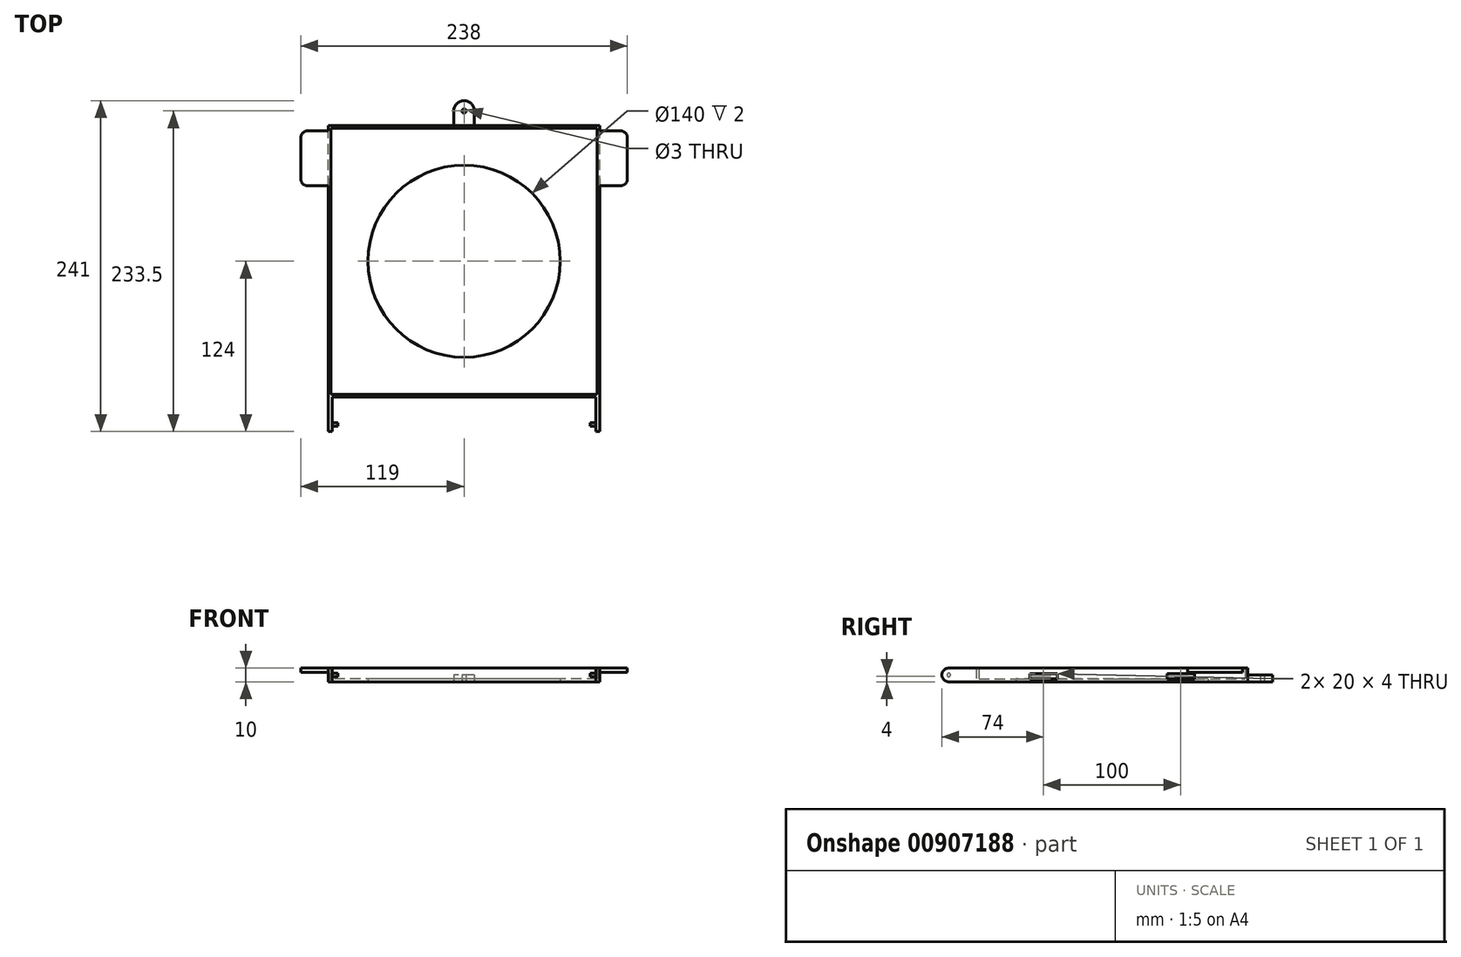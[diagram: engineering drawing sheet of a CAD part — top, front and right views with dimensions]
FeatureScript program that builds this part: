
annotation { "Feature Type Name" : "Feature", "Feature Type Description" : "" }
export const myFeature = defineFeature(function(context is Context, id is Id, definition is map)
    precondition{}
    {
        {
            var Q0;
            Q0=qCreatedBy(makeId("Top.planeOp"),FACE);
            var sketch = newSketch(context, id + "F0", { "sketchPlane" : qUnion([Q0])});
            skLineSegment(sketch, "E0.bottom", {"start": v(97, -97) * mm, "end": v(-97, -97) * mm});
            skLineSegment(sketch, "E0.top", {"start": v(97, 97) * mm, "end": v(-97, 97) * mm});
            skLineSegment(sketch, "E0.left", {"start": v(97, -97) * mm, "end": v(97, 97) * mm});
            skLineSegment(sketch, "E0.right", {"start": v(-97, -97) * mm, "end": v(-97, 97) * mm});
            skPoint(sketch, "E0.middle", {"position": v(0, 0) * mm});
            skLineSegment(sketch, "E1.bottom", {"start": v(99, -99) * mm, "end": v(-99, -99) * mm});
            skLineSegment(sketch, "E1.top", {"start": v(99, 99) * mm, "end": v(-99, 99) * mm});
            skLineSegment(sketch, "E1.left", {"start": v(99, -99) * mm, "end": v(99, 99) * mm});
            skLineSegment(sketch, "E1.right", {"start": v(-99, -99) * mm, "end": v(-99, 99) * mm});
            skCircle(sketch, "E2", {"center": v(0, 0) * mm, "radius": 70 * mm});
            skLineSegment(sketch, "E3.bottom", {"start": v(-99, -99) * mm, "end": v(-96, -99) * mm});
            skLineSegment(sketch, "E3.top", {"start": v(-99, -119) * mm, "end": v(-96, -119) * mm});
            skLineSegment(sketch, "E3.left", {"start": v(-99, -99) * mm, "end": v(-99, -119) * mm});
            skLineSegment(sketch, "E3.right", {"start": v(-96, -99) * mm, "end": v(-96, -119) * mm});
            skLineSegment(sketch, "E4.MirrorCS", {"start": v(99, -99) * mm, "end": v(99, -119) * mm});
            skLineSegment(sketch, "E5.MirrorCS", {"start": v(96, -99) * mm, "end": v(96, -119) * mm});
            skLineSegment(sketch, "E6.MirrorCS", {"start": v(99, -119) * mm, "end": v(96, -119) * mm});
            skLineSegment(sketch, "E7.bottom", {"start": v(-7.5, 99) * mm, "end": v(7.5, 99) * mm});
            skLineSegment(sketch, "E7.left", {"start": v(-7.5, 99) * mm, "end": v(-7.5, 109.5) * mm});
            skLineSegment(sketch, "E7.right", {"start": v(7.5, 99) * mm, "end": v(7.5, 109.5) * mm});
            skArc(sketch, "E8", {"start": v(7.5, 109.5) * mm, "mid": v(0, 117) * mm, "end": v(-7.5, 109.5) * mm});
            skCircle(sketch, "E9", {"center": v(0, 109.5) * mm, "radius": 1.5 * mm});
            skSolve(sketch);
        }
        {
            var Q0;
            Q0=makeQuery(id+"F0.imprint","IMPRINT",FACE,{"disambiguationData":[TD([[makeQuery(id+"F0.imprint","IMPRINT",EDGE,{"derivedFrom":sQuery(id+"F0.wireOp",EDGE,"E0.bottom")}),-1.0]])]});
            extrude(context, id + "F1", {"entities" : qUnion([Q0]), "depth" : 2 * mm});
        }
        {
            var Q0;
            {var subQ1=sQuery(id+"F0.wireOp",EDGE,"E7.left");Q0=makeQuery(id+"F0.imprint","IMPRINT",FACE,{"disambiguationData":[TD([[makeQuery(id+"F0.imprint","IMPRINT",EDGE,{"derivedFrom":subQ1}),-1.0]])]});}
            extrude(context, id + "F2", {"entities" : qUnion([Q0]), "operationType" : NewBodyOperationType.ADD, "depth" : 5 * mm});
        }
        {
            var Q0;
            Q0=makeQuery(id+"F0.imprint","IMPRINT",FACE,{"disambiguationData":[TD([[makeQuery(id+"F0.imprint","IMPRINT",EDGE,{"derivedFrom":sQuery(id+"F0.wireOp",EDGE,"E0.bottom")}),1.0]])]});
            var Q1;
            Q1=makeQuery(id+"F0.imprint","IMPRINT",FACE,{"disambiguationData":[TD([[makeQuery(id+"F0.imprint","IMPRINT",EDGE,{"derivedFrom":sQuery(id+"F0.wireOp",EDGE,"E3.top")}),1.0]])]});
            var Q2;
            {var subQ2=sQuery(id+"F0.wireOp",EDGE,"E4.MirrorCS");Q2=makeQuery(id+"F0.imprint","IMPRINT",FACE,{"disambiguationData":[TD([[makeQuery(id+"F0.imprint","IMPRINT",EDGE,{"derivedFrom":subQ2}),-1.0]])]});}
            extrude(context, id + "F3", {"entities" : qUnion([Q0, Q1, Q2]), "operationType" : NewBodyOperationType.ADD, "depth" : 10 * mm});
        }
        {
            var Q0;
            Q0=makeQuery(id+"F3.opExtrude","SWEPT_FACE",FACE,{"disambiguationData":[OSD([sQuery(id+"F0.wireOp",EDGE,"E3.right")])]});
            var sketch = newSketch(context, id + "F4", { "sketchPlane" : qUnion([Q0])});
            skArc(sketch, "E10", {"start": v(-119, 10) * mm, "mid": v(-124, 5) * mm, "end": v(-119, 0) * mm});
            skSolve(sketch);
        }
        {
            var Q0;
            Q0=qSketchRegion(id+"F4",true);
            var Q1;
            Q1=makeQuery(id+"F4.imprint","IMPRINT",FACE,{"disambiguationData":[TD([[makeQuery(id+"F4.imprint","IMPRINT",EDGE,{"derivedFrom":sQuery(id+"F4.wireOp",EDGE,"E10")}),1.0]])]});
            extrude(context, id + "F5", {"entities" : qUnion([Q0, Q1]), "operationType" : NewBodyOperationType.ADD, "oppositeDirection" : true, "depth" : 3 * mm});
        }
        {
            var Q0;
            Q0=makeQuery(id+"F3.opExtrude","SWEPT_FACE",FACE,{"disambiguationData":[OSD([sQuery(id+"F0.wireOp",EDGE,"E1.left"),sQuery(id+"F0.wireOp",EDGE,"E4.MirrorCS")])]});
            var sketch = newSketch(context, id + "F6", { "sketchPlane" : qUnion([Q0])});
            skArc(sketch, "E11", {"start": v(-119, 10) * mm, "mid": v(-124, 5) * mm, "end": v(-119, 0) * mm});
            skSolve(sketch);
        }
        {
            var Q0;
            Q0=qSketchRegion(id+"F6",true);
            var Q1;
            Q1=makeQuery(id+"F6.imprint","IMPRINT",FACE,{"disambiguationData":[TD([[makeQuery(id+"F6.imprint","IMPRINT",EDGE,{"derivedFrom":sQuery(id+"F6.wireOp",EDGE,"E11")}),1.0]])]});
            extrude(context, id + "F7", {"entities" : qUnion([Q0, Q1]), "operationType" : NewBodyOperationType.ADD, "oppositeDirection" : true, "depth" : 3 * mm});
        }
        {
            var Q0;
            {var subQ0=sQuery(id+"F0.wireOp",EDGE,"E3.right");Q0=makeQuery(id+"F5.boolean.opBoolean","MERGE",FACE,{"derivedFrom":[makeQuery(id+"F3.opExtrude","SWEPT_FACE",FACE,{"disambiguationData":[OSD([subQ0])]}),makeQuery(id+"F5.opExtrude","CAP_FACE",FACE,{"disambiguationData":[OSD([sQuery(id+"F0.wireOp",EDGE,"E3.top"),subQ0,sQuery(id+"F4.wireOp",EDGE,"E10")])],"isStart":true})]});}
            var sketch = newSketch(context, id + "F8", { "sketchPlane" : qUnion([Q0])});
            skCircle(sketch, "E12", {"center": v(-119, 5) * mm, "radius": 1.25 * mm});
            skSolve(sketch);
        }
        {
            var Q0;
            Q0=makeQuery(id+"F8.imprint","IMPRINT",FACE,{"disambiguationData":[TD([[makeQuery(id+"F8.imprint","IMPRINT",EDGE,{"derivedFrom":sQuery(id+"F8.wireOp",EDGE,"E12")}),1.0]])]});
            extrude(context, id + "F9", {"entities" : qUnion([Q0]), "operationType" : NewBodyOperationType.ADD, "depth" : 4 * mm});
        }
        {
            var Q0;
            Q0=makeQuery(id+"F7.boolean.opBoolean","MERGE",FACE,{"derivedFrom":[makeQuery(id+"F3.opExtrude","SWEPT_FACE",FACE,{"disambiguationData":[OSD([sQuery(id+"F0.wireOp",EDGE,"E5.MirrorCS")])]}),makeQuery(id+"F7.opExtrude","CAP_FACE",FACE,{"disambiguationData":[OSD([sQuery(id+"F0.wireOp",EDGE,"E4.MirrorCS"),sQuery(id+"F0.wireOp",EDGE,"E6.MirrorCS"),sQuery(id+"F6.wireOp",EDGE,"E11")])],"isStart":false})]});
            cPlane(context, id + "F10", {"entities" : qUnion([Q0]), "cplaneType" : CPlaneType.OFFSET, "offset" : 0 * mm, "width" : 150 * mm, "height" : 150 * mm});
        }
        {
            var Q0;
            Q0=qCreatedBy(id+"F10.planeOp",FACE);
            var sketch = newSketch(context, id + "F11", { "sketchPlane" : qUnion([Q0])});
            skCircle(sketch, "E13.0", {"center": v(119, 5) * mm, "radius": 1.25 * mm});
            skSolve(sketch);
        }
        {
            var Q0;
            Q0=makeQuery(id+"F11.imprint","IMPRINT",FACE,{"disambiguationData":[TD([[makeQuery(id+"F11.imprint","IMPRINT",EDGE,{"derivedFrom":sQuery(id+"F11.wireOp",EDGE,"E13.0")}),1.0]])]});
            extrude(context, id + "F12", {"entities" : qUnion([Q0]), "operationType" : NewBodyOperationType.ADD, "depth" : 4 * mm});
        }
        {
            var Q0;
            Q0=makeQuery(id+"F3.opExtrude","CAP_FACE",FACE,{"disambiguationData":[OSD([sQuery(id+"F0.wireOp",EDGE,"E0.bottom"),sQuery(id+"F0.wireOp",EDGE,"E0.top"),sQuery(id+"F0.wireOp",EDGE,"E0.left"),sQuery(id+"F0.wireOp",EDGE,"E0.right"),sQuery(id+"F0.wireOp",EDGE,"E1.bottom"),sQuery(id+"F0.wireOp",EDGE,"E1.top"),sQuery(id+"F0.wireOp",EDGE,"E1.left"),sQuery(id+"F0.wireOp",EDGE,"E1.right"),sQuery(id+"F0.wireOp",EDGE,"E3.top"),sQuery(id+"F0.wireOp",EDGE,"E3.left"),sQuery(id+"F0.wireOp",EDGE,"E3.right"),sQuery(id+"F0.wireOp",EDGE,"E4.MirrorCS"),sQuery(id+"F0.wireOp",EDGE,"E5.MirrorCS"),sQuery(id+"F0.wireOp",EDGE,"E6.MirrorCS")])],"isStart":false});
            var sketch = newSketch(context, id + "F13", { "sketchPlane" : qUnion([Q0])});
            skLineSegment(sketch, "E14.bottom", {"start": v(-99, 95) * mm, "end": v(-114, 95) * mm});
            skLineSegment(sketch, "E14.top", {"start": v(-99, 55) * mm, "end": v(-114, 55) * mm});
            skLineSegment(sketch, "E14.left", {"start": v(-99, 95) * mm, "end": v(-99, 55) * mm});
            skLineSegment(sketch, "E14.right", {"start": v(-119, 90) * mm, "end": v(-119, 60) * mm});
            skPoint(sketch, "E15.visualSharp", {"position": v(-119, 95) * mm});
            skArc(sketch, "E15.filletArc", {"start": v(-114, 95) * mm, "mid": v(-117.54, 93.54) * mm, "end": v(-119, 90) * mm});
            skPoint(sketch, "E16.visualSharp", {"position": v(-119, 55) * mm});
            skArc(sketch, "E16.filletArc", {"start": v(-119, 60) * mm, "mid": v(-117.54, 56.46) * mm, "end": v(-114, 55) * mm});
            skLineSegment(sketch, "E17.MirrorCS", {"start": v(99, 95) * mm, "end": v(114, 95) * mm});
            skArc(sketch, "E18.MirrorCS", {"start": v(114, 95) * mm, "mid": v(117.54, 93.54) * mm, "end": v(119, 90) * mm});
            skLineSegment(sketch, "E19.MirrorCS", {"start": v(119, 90) * mm, "end": v(119, 60) * mm});
            skArc(sketch, "E20.MirrorCS", {"start": v(119, 60) * mm, "mid": v(117.54, 56.46) * mm, "end": v(114, 55) * mm});
            skLineSegment(sketch, "E21.MirrorCS", {"start": v(99, 55) * mm, "end": v(114, 55) * mm});
            skSolve(sketch);
        }
        {
            var Q0;
            Q0=qSketchRegion(id+"F13",true);
            var Q1;
            {var subQ0=sQuery(id+"F13.wireOp",EDGE,"E17.MirrorCS");Q1=makeQuery(id+"F13.imprint","IMPRINT",FACE,{"disambiguationData":[TD([[makeQuery(id+"F13.imprint","IMPRINT",EDGE,{"derivedFrom":subQ0}),-1.0]])]});}
            extrude(context, id + "F14", {"entities" : qUnion([Q0, Q1]), "operationType" : NewBodyOperationType.ADD, "oppositeDirection" : true, "depth" : 3 * mm});
        }
        {
            var Q0;
            Q0=makeQuery(id+"F3.opExtrude","SWEPT_FACE",FACE,{"disambiguationData":[OSD([sQuery(id+"F0.wireOp",EDGE,"E0.right")])]});
            var sketch = newSketch(context, id + "F15", { "sketchPlane" : qUnion([Q0])});
            skLineSegment(sketch, "E22.bottom", {"start": v(60, 2) * mm, "end": v(40, 2) * mm});
            skLineSegment(sketch, "E22.top", {"start": v(60, 6) * mm, "end": v(40, 6) * mm});
            skLineSegment(sketch, "E22.left", {"start": v(60, 2) * mm, "end": v(60, 6) * mm});
            skLineSegment(sketch, "E22.right", {"start": v(40, 2) * mm, "end": v(40, 6) * mm});
            skLineSegment(sketch, "E23.MirrorCS", {"start": v(-60, 6) * mm, "end": v(-40, 6) * mm});
            skLineSegment(sketch, "E24.MirrorCS", {"start": v(-40, 2) * mm, "end": v(-40, 6) * mm});
            skLineSegment(sketch, "E25.MirrorCS", {"start": v(-60, 2) * mm, "end": v(-60, 6) * mm});
            skPoint(sketch, "E26", {"position": v(-50, 6) * mm});
            skPoint(sketch, "E27", {"position": v(50, 6) * mm});
            skSolve(sketch);
        }
        {
            var Q0;
            Q0=makeQuery(id+"F15.imprint","IMPRINT",FACE,{"disambiguationData":[TD([[makeQuery(id+"F15.imprint","IMPRINT",EDGE,{"derivedFrom":sQuery(id+"F15.wireOp",EDGE,"E23.MirrorCS")}),-1.0]])]});
            var Q1;
            Q1=makeQuery(id+"F15.imprint","IMPRINT",FACE,{"disambiguationData":[TD([[makeQuery(id+"F15.imprint","IMPRINT",EDGE,{"derivedFrom":sQuery(id+"F15.wireOp",EDGE,"E22.bottom")}),1.0]])]});
            extrude(context, id + "F16", {"entities" : qUnion([Q0, Q1]), "operationType" : NewBodyOperationType.REMOVE, "endBound" : BoundingType.UP_TO_NEXT, "oppositeDirection" : true, "depth" : 25 * mm});
        }
        {
            var Q0;
            Q0=makeQuery(id+"F3.opExtrude","SWEPT_FACE",FACE,{"disambiguationData":[OSD([sQuery(id+"F0.wireOp",EDGE,"E0.left")])]});
            var sketch = newSketch(context, id + "F17", { "sketchPlane" : qUnion([Q0])});
            skLineSegment(sketch, "E28.0", {"start": v(-60, 6) * mm, "end": v(-40, 6) * mm});
            skLineSegment(sketch, "E29.0", {"start": v(-40, 2) * mm, "end": v(-40, 6) * mm});
            skLineSegment(sketch, "E30.0", {"start": v(-60, 2) * mm, "end": v(-60, 6) * mm});
            skLineSegment(sketch, "E31.0", {"start": v(40, 2) * mm, "end": v(40, 6) * mm});
            skLineSegment(sketch, "E32.0", {"start": v(60, 6) * mm, "end": v(40, 6) * mm});
            skLineSegment(sketch, "E33.0", {"start": v(60, 2) * mm, "end": v(60, 6) * mm});
            skSolve(sketch);
        }
        {
            var Q0;
            {var subQ0=sQuery(id+"F17.wireOp",EDGE,"E31.0");Q0=makeQuery(id+"F17.imprint","IMPRINT",FACE,{"disambiguationData":[TD([[makeQuery(id+"F17.imprint","IMPRINT",EDGE,{"derivedFrom":subQ0}),-1.0]])]});}
            var Q1;
            Q1=makeQuery(id+"F17.imprint","IMPRINT",FACE,{"disambiguationData":[TD([[makeQuery(id+"F17.imprint","IMPRINT",EDGE,{"derivedFrom":sQuery(id+"F17.wireOp",EDGE,"E28.0")}),-1.0]])]});
            extrude(context, id + "F18", {"entities" : qUnion([Q0, Q1]), "operationType" : NewBodyOperationType.REMOVE, "endBound" : BoundingType.UP_TO_NEXT, "oppositeDirection" : true, "depth" : 25 * mm});
        }
    });
